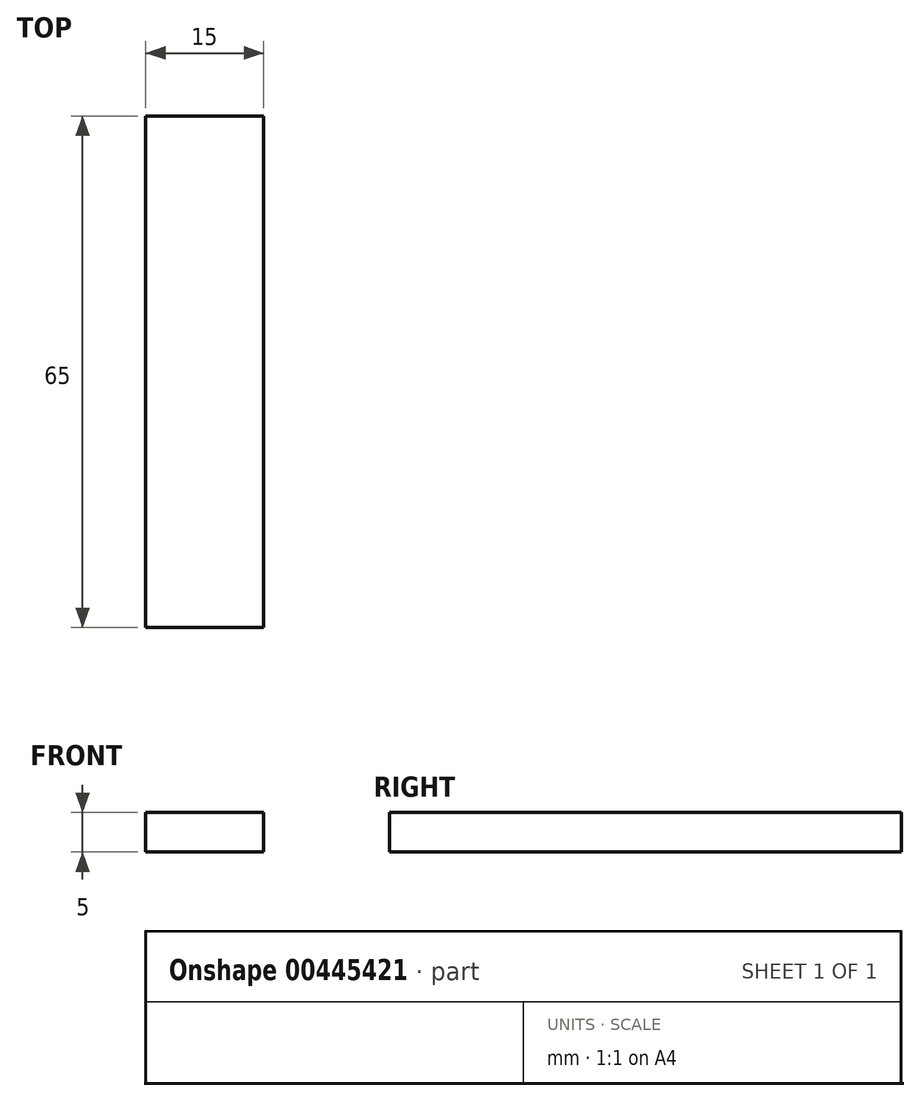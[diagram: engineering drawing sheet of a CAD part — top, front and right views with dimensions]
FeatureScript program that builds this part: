
annotation { "Feature Type Name" : "Feature", "Feature Type Description" : "" }
export const myFeature = defineFeature(function(context is Context, id is Id, definition is map)
    precondition{}
    {
        {
            var Q0;
            Q0=qCreatedBy(makeId("Front.planeOp"),FACE);
            var sketch = newSketch(context, id + "F0", { "sketchPlane" : qUnion([Q0])});
            skLineSegment(sketch, "E0.bottom", {"start": v(7.5, 2.5) * mm, "end": v(-7.5, 2.5) * mm});
            skLineSegment(sketch, "E0.top", {"start": v(7.5, -2.5) * mm, "end": v(-7.5, -2.5) * mm});
            skLineSegment(sketch, "E0.left", {"start": v(7.5, 2.5) * mm, "end": v(7.5, -2.5) * mm});
            skLineSegment(sketch, "E0.right", {"start": v(-7.5, 2.5) * mm, "end": v(-7.5, -2.5) * mm});
            skPoint(sketch, "E0.middle", {"position": v(0, 0) * mm});
            skSolve(sketch);
        }
        {
            var Q0;
            Q0=makeQuery(id+"F0.imprint","IMPRINT",FACE,{"disambiguationData":[TD([[makeQuery(id+"F0.imprint","IMPRINT",EDGE,{"derivedFrom":sQuery(id+"F0.wireOp",EDGE,"E0.bottom")}),1.0]])]});
            extrude(context, id + "F1", {"entities" : qUnion([Q0]), "depth" : 65 * mm});
        }
        {
            var Q0;
            Q0=makeQuery(id+"F1.opExtrude","SWEPT_FACE",FACE,{"disambiguationData":[OSD([sQuery(id+"F0.wireOp",EDGE,"E0.top")])]});
            var sketch = newSketch(context, id + "F2", { "sketchPlane" : qUnion([Q0])});
            skPoint(sketch, "E1", {"position": v(0, 32.5) * mm});
            skPoint(sketch, "E1.positionSnap0", {"position": v(-7.5, 32.5) * mm});
            skPoint(sketch, "E2", {"position": v(0, 57.5) * mm});
            skPoint(sketch, "E3", {"position": v(0, 7.5) * mm});
            skSolve(sketch);
        }
    });
